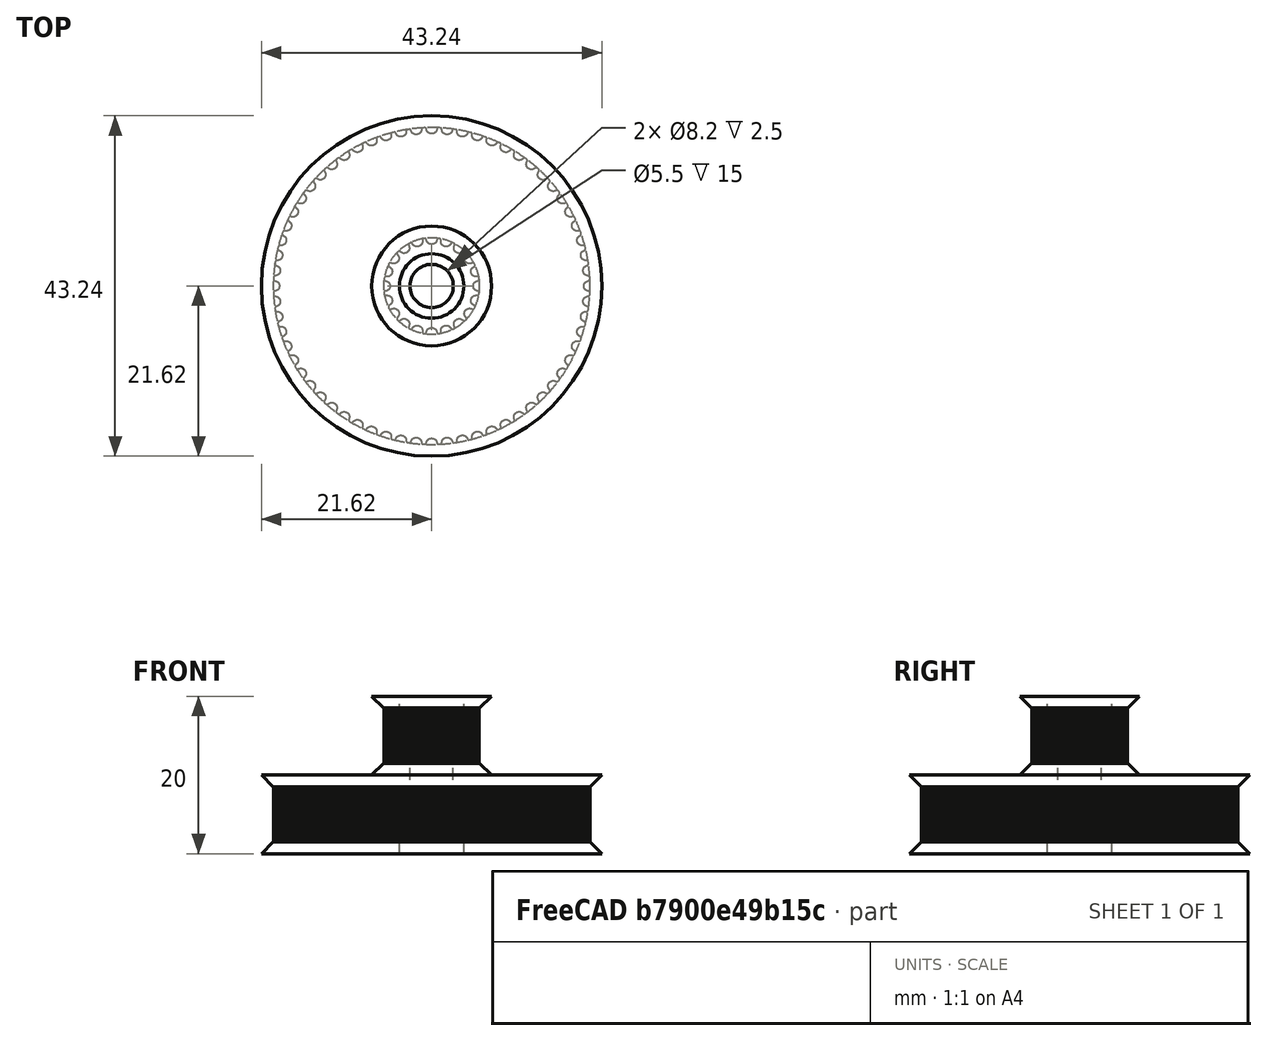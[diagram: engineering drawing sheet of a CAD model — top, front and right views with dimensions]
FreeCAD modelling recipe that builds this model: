
FCSTD DOCUMENT  (FreeCAD 0.18R16146 (Git))
Label: 20-40-pulley
License: All rights reserved
LicenseURL: http://en.wikipedia.org/wiki/All_rights_reserved
objects: Part::Cylinder×9, Part::Feature×7, Part::MultiFuse×5, Part::Cut×5
note: 26 computed .brp shape members not serialized (recipe doc carries the construction recipe); baked Part::Feature solids carry a one-line shape summary decoded from their .brp

FEATURE [Part::Feature] difference001_solid  label="20-teeth"
  Placement = pos=(0,0,10) rot=(0,0,1;0rad)
  shape: bbox 15.22 x 15.22 x 10 mm, 505 faces (baked)
FEATURE [Part::Feature] difference003_solid  label="40-teeth"
  shape: bbox 27.96 x 27.96 x 10 mm, 985 faces (baked)
FEATURE [Part::Cylinder] Cylinder002
  Angle = 360
  AttacherType = Attacher::AttachEngine3D
  Height = 20.5
  Placement = pos=(0,0,-1.5) rot=(0,0,1;0rad)
  Radius = 2.75
FEATURE [Part::MultiFuse] Fusion
  Shapes = -> [difference003_solid,difference001_solid]
FEATURE [Part::Cut] Cut
  Base = -> Fusion
  Tool = -> Cylinder002
FEATURE [Part::Cylinder] Cylinder
  Angle = 360
  AttacherType = Attacher::AttachEngine3D
  Height = 2.5
  Placement = pos=(0,0,-1.5) rot=(0,0,1;0rad)
  Radius = 4.1
FEATURE [Part::Cylinder] Cylinder003
  Angle = 360
  AttacherType = Attacher::AttachEngine3D
  Height = 2.5
  Placement = pos=(0,0,16) rot=(0,0,1;0rad)
  Radius = 4.1
FEATURE [Part::MultiFuse] Fusion001
  Shapes = -> [Cylinder,Cylinder003]
FEATURE [Part::Cut] Cut001
  Base = -> Cut
  Placement = pos=(0,0,1.5) rot=(0,0,1;0rad)
  Tool = -> Fusion001
FEATURE [Part::Feature] Cut001001  label="4020-idler"
  shape: bbox 27.96 x 27.96 x 20 mm, 1452 faces (baked)
FEATURE [Part::Cylinder] Cylinder004
  Angle = 360
  AttacherType = Attacher::AttachEngine3D
  Height = 0.6
  Radius = 4.6
FEATURE [Part::Cylinder] Cylinder005
  Angle = 360
  AttacherType = Attacher::AttachEngine3D
  Height = 2.5
  Radius = 4
FEATURE [Part::Cylinder] Cylinder006
  Angle = 360
  AttacherType = Attacher::AttachEngine3D
  Height = 6
  Radius = 2.5
FEATURE [Part::MultiFuse] Fusion002
  Shapes = -> [Cylinder005,Cylinder004]
FEATURE [Part::Cut] Cut001002
  Base = -> Fusion002
  Tool = -> Cylinder006
FEATURE [Part::Feature] Cut001002001  label="SMF85ZZ-bearing"
  shape: bbox 9.2 x 9.2 x 2.5 mm, 6 faces (baked)
FEATURE [Part::Feature] difference001001  label="difference002"
  shape: bbox 43.24 x 43.24 x 10 mm, 1561 faces (baked)
FEATURE [Part::Feature] difference001_solid001  label="20-teeth001"
  Placement = pos=(0,0,10) rot=(0,0,1;0rad)
  shape: bbox 15.22 x 15.22 x 10 mm, 505 faces (baked)
FEATURE [Part::Cylinder] Cylinder007
  Angle = 360
  AttacherType = Attacher::AttachEngine3D
  Height = 32
  Placement = pos=(0,0,-4) rot=(0,0,1;0rad)
  Radius = 2.75
FEATURE [Part::MultiFuse] Fusion003
  Shapes = -> [difference001_solid001,difference001001]
FEATURE [Part::Cut] Cut001002002
  Base = -> Fusion003
  Tool = -> Cylinder007
FEATURE [Part::Cylinder] Cylinder008
  Angle = 360
  AttacherType = Attacher::AttachEngine3D
  Height = 2.5
  Placement = pos=(0,0,-1.5) rot=(0,0,1;0rad)
  Radius = 4.1
FEATURE [Part::Cylinder] Cylinder009
  Angle = 360
  AttacherType = Attacher::AttachEngine3D
  Height = 2.5
  Placement = pos=(0,0,16) rot=(0,0,1;0rad)
  Radius = 4.1
FEATURE [Part::MultiFuse] Fusion004
  Shapes = -> [Cylinder009,Cylinder008]
FEATURE [Part::Cut] Cut001002003
  Base = -> Cut001002002
  Placement = pos=(0,0,1.5) rot=(0,0,1;0rad)
  Tool = -> Fusion004
FEATURE [Part::Feature] Cut001002003001  label="64-20-idler"
  shape: bbox 43.24 x 43.24 x 20 mm, 2028 faces (baked)
